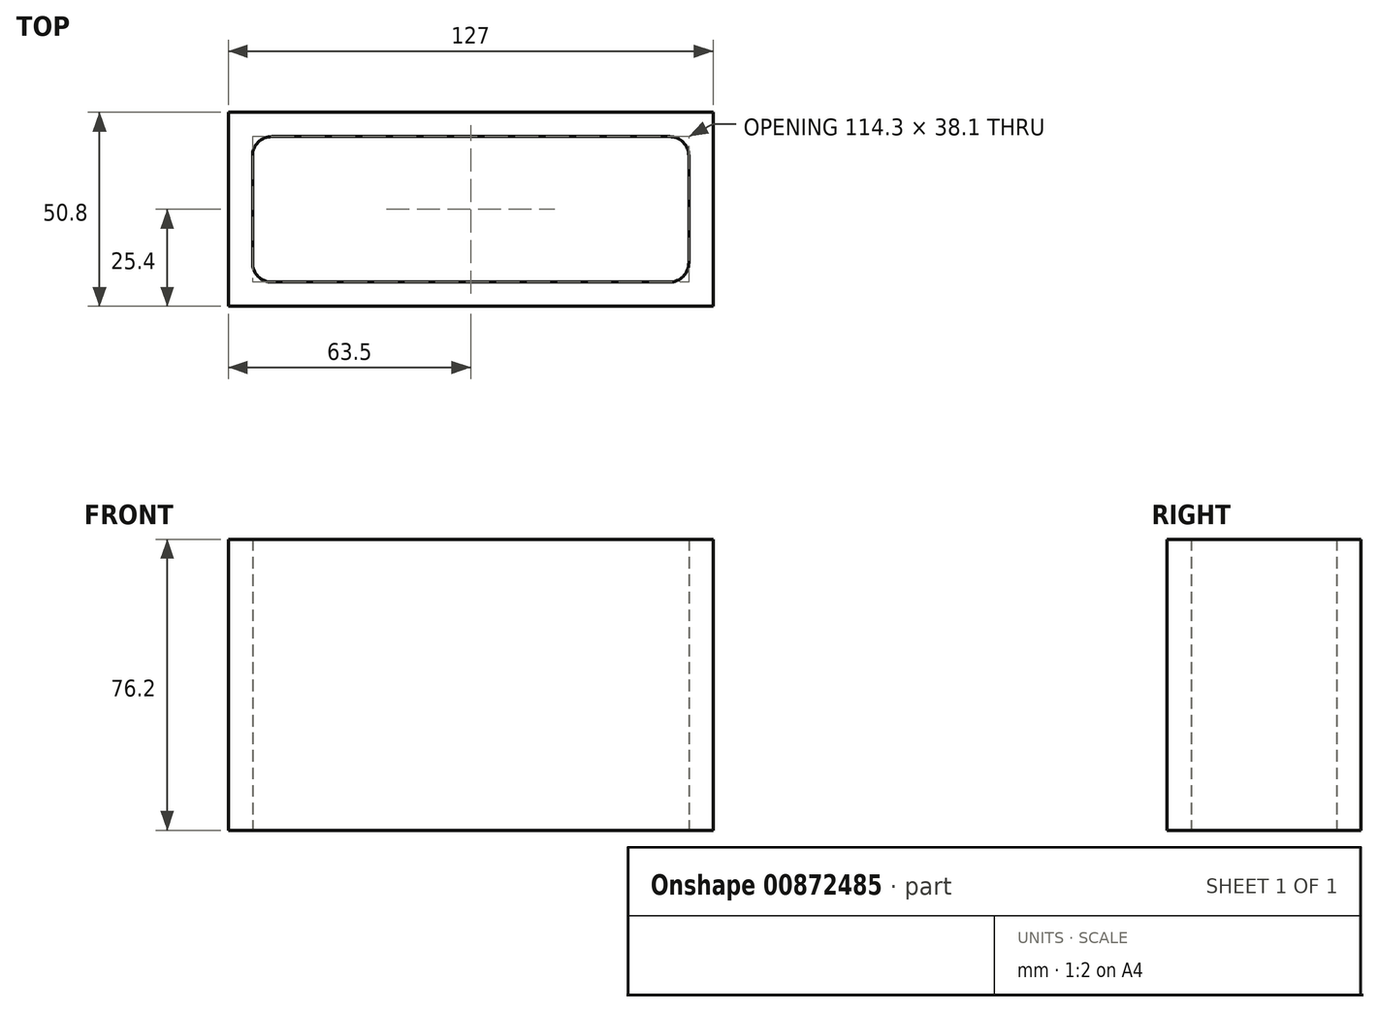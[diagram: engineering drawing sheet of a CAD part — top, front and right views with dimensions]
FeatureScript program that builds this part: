
annotation { "Feature Type Name" : "Feature", "Feature Type Description" : "" }
export const myFeature = defineFeature(function(context is Context, id is Id, definition is map)
    precondition{}
    {
        {
            var Q0;
            Q0=qCreatedBy(makeId("Top.planeOp"),FACE);
            var sketch = newSketch(context, id + "F0", { "sketchPlane" : qUnion([Q0])});
            skLineSegment(sketch, "E0", {"start": v(0, 0) * mm, "end": v(63.5, 0) * mm});
            skLineSegment(sketch, "E1", {"start": v(63.5, 0) * mm, "end": v(63.5, 50.8) * mm});
            skLineSegment(sketch, "E2", {"start": v(63.5, 50.8) * mm, "end": v(0, 50.8) * mm});
            skLineSegment(sketch, "E3", {"start": v(0, 6.35) * mm, "end": v(57.15, 6.35) * mm});
            skLineSegment(sketch, "E4", {"start": v(57.15, 6.35) * mm, "end": v(57.15, 44.45) * mm});
            skLineSegment(sketch, "E5", {"start": v(57.15, 44.45) * mm, "end": v(0, 44.45) * mm});
            skLineSegment(sketch, "E6.MirrorCS", {"start": v(-57.15, 44.45) * mm, "end": v(0, 44.45) * mm});
            skLineSegment(sketch, "E7.MirrorCS", {"start": v(-63.5, 50.8) * mm, "end": v(0, 50.8) * mm});
            skLineSegment(sketch, "E8.MirrorCS", {"start": v(-57.15, 6.35) * mm, "end": v(-57.15, 44.45) * mm});
            skLineSegment(sketch, "E9.MirrorCS", {"start": v(-63.5, 0) * mm, "end": v(-63.5, 50.8) * mm});
            skLineSegment(sketch, "E10.MirrorCS", {"start": v(0, 0) * mm, "end": v(-63.5, 0) * mm});
            skLineSegment(sketch, "E11.MirrorCS", {"start": v(0, 6.35) * mm, "end": v(-57.15, 6.35) * mm});
            skSolve(sketch);
        }
        {
            var Q0;
            Q0=makeQuery(id+"F0.imprint","IMPRINT",FACE,{"disambiguationData":[TD([[makeQuery(id+"F0.imprint","IMPRINT",EDGE,{"derivedFrom":sQuery(id+"F0.wireOp",EDGE,"E0")}),1.0]])]});
            extrude(context, id + "F1", {"entities" : qUnion([Q0]), "depth" : 76.2 * mm, "offsetDistance" : 25.4 * mm});
        }
        {
            var Q0;
            Q0=makeQuery(id+"F1.opExtrude","SWEPT_EDGE",EDGE,{"disambiguationData":[OSD([sQuery(id+"F0.wireOp",EDGE,"E6.MirrorCS"),sQuery(id+"F0.wireOp",EDGE,"E8.MirrorCS")])]});
            var Q1;
            Q1=makeQuery(id+"F1.opExtrude","SWEPT_EDGE",EDGE,{"disambiguationData":[OSD([sQuery(id+"F0.wireOp",EDGE,"E4"),sQuery(id+"F0.wireOp",EDGE,"E5")])]});
            var Q2;
            Q2=makeQuery(id+"F1.opExtrude","SWEPT_EDGE",EDGE,{"disambiguationData":[OSD([sQuery(id+"F0.wireOp",EDGE,"E8.MirrorCS"),sQuery(id+"F0.wireOp",EDGE,"E11.MirrorCS")])]});
            var Q3;
            Q3=makeQuery(id+"F1.opExtrude","SWEPT_EDGE",EDGE,{"disambiguationData":[OSD([sQuery(id+"F0.wireOp",EDGE,"E3"),sQuery(id+"F0.wireOp",EDGE,"E4")])]});
            fillet(context, id + "F2", {"entities" : qUnion([Q0, Q1, Q2, Q3]), "radius" : 5.08 * mm, "tangentPropagation" : true, "allowEdgeOverflow" : false});
        }
    });
